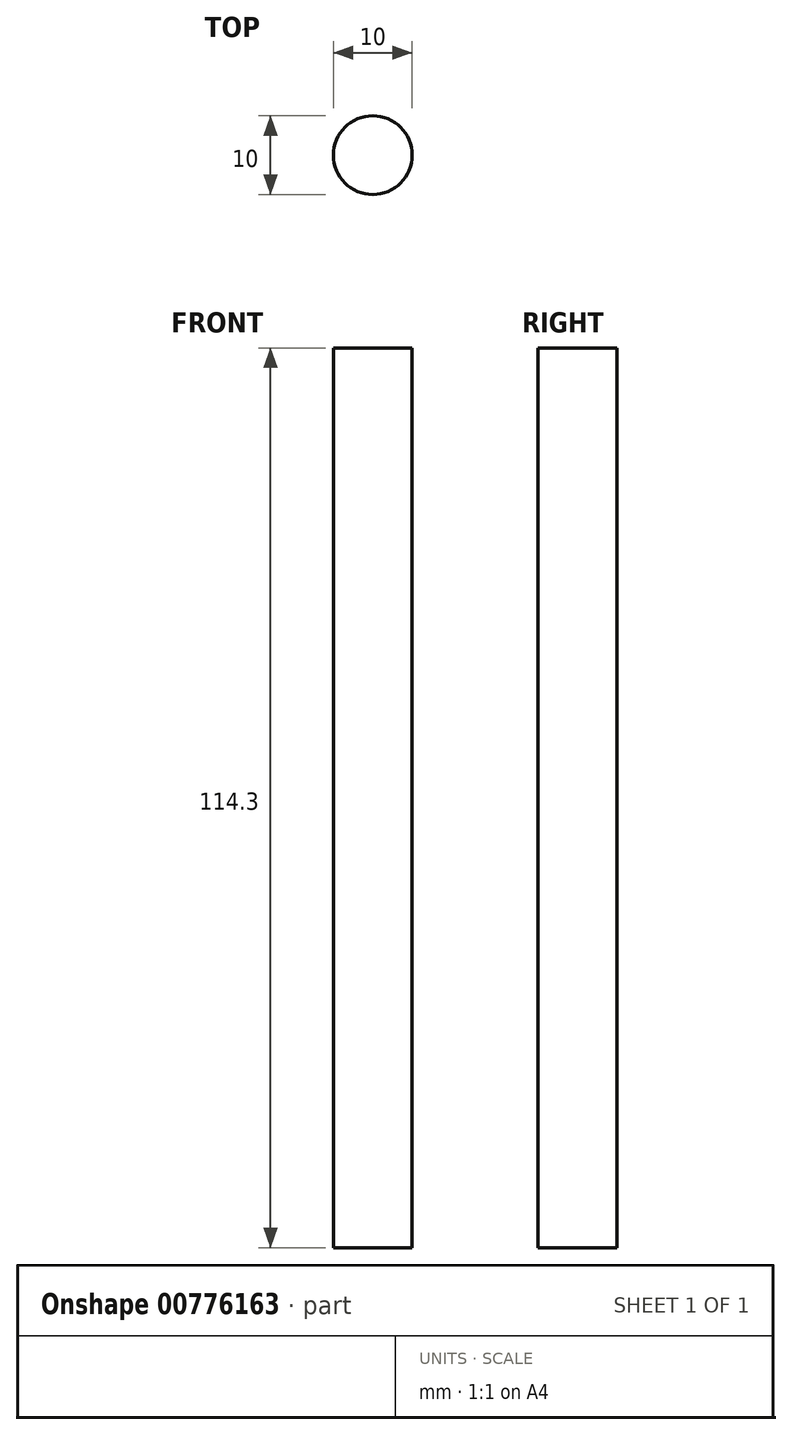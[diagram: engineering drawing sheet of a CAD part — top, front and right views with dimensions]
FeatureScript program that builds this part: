
annotation { "Feature Type Name" : "Feature", "Feature Type Description" : "" }
export const myFeature = defineFeature(function(context is Context, id is Id, definition is map)
    precondition{}
    {
        {
            var Q0;
            Q0=qCreatedBy(makeId("Top.planeOp"),FACE);
            var sketch = newSketch(context, id + "F0", { "sketchPlane" : qUnion([Q0])});
            skCircle(sketch, "E0", {"center": v(0, 0) * mm, "radius": 5 * mm});
            skSolve(sketch);
        }
        {
            var Q0;
            Q0 = qSketchRegion(id + "F0", true);
            extrude(context, id + "F1", {"entities" : qUnion([Q0]), "depth" : 114.3 * mm, "offsetDistance" : 25.4 * mm});
        }
    });
